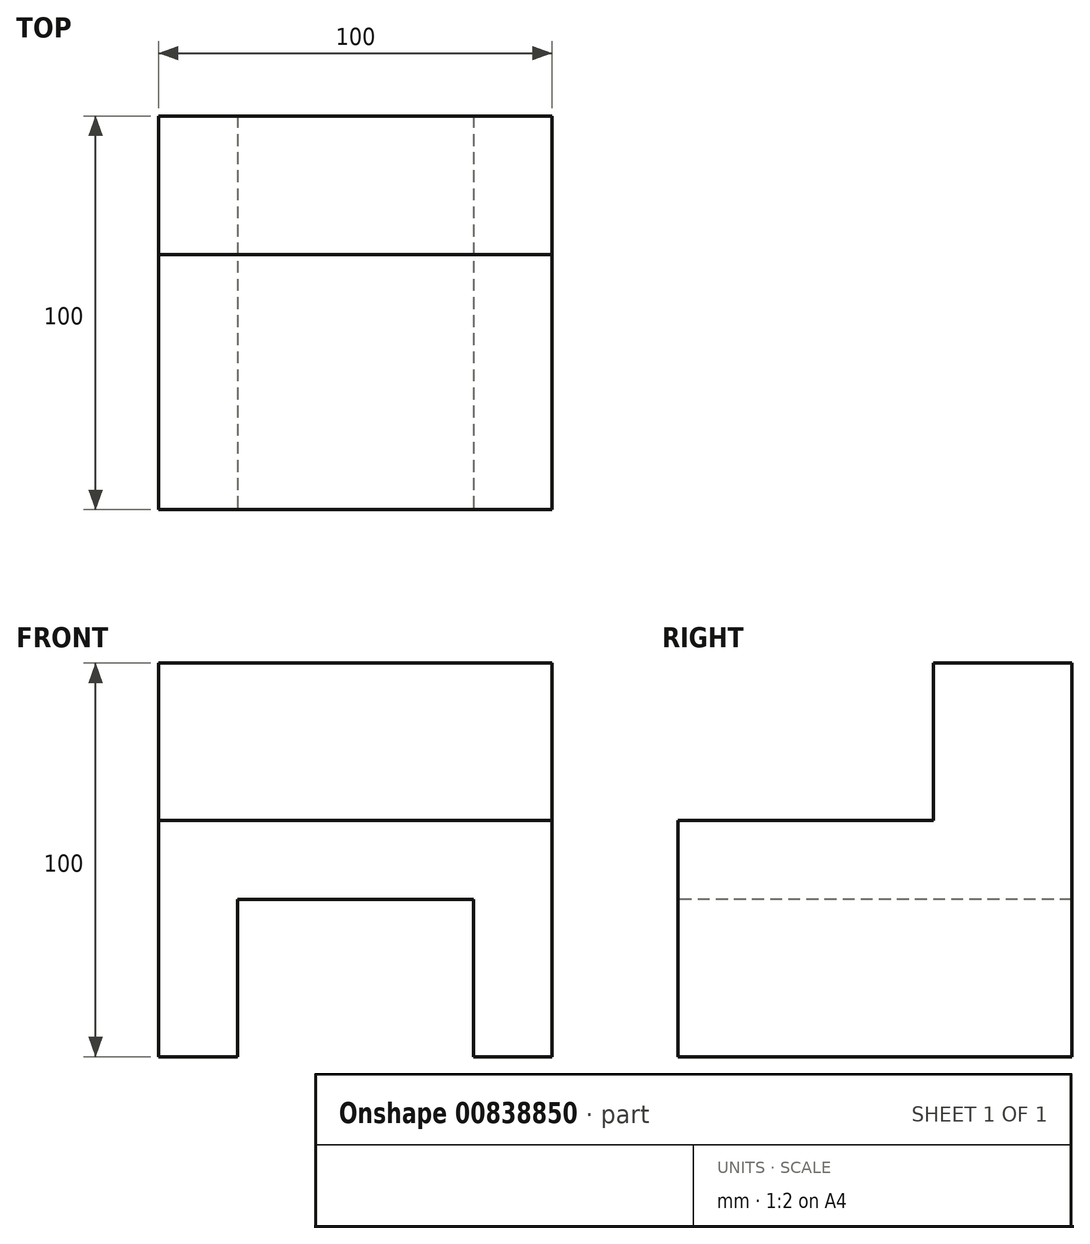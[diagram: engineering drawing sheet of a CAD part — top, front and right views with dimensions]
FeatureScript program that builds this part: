
annotation { "Feature Type Name" : "Feature", "Feature Type Description" : "" }
export const myFeature = defineFeature(function(context is Context, id is Id, definition is map)
    precondition{}
    {
        {
            var Q0;
            Q0=qCreatedBy(makeId("Top.planeOp"),FACE);
            var sketch = newSketch(context, id + "F0", { "sketchPlane" : qUnion([Q0])});
            skLineSegment(sketch, "E0.bottom", {"start": v(50, -50) * mm, "end": v(-50, -50) * mm});
            skLineSegment(sketch, "E0.top", {"start": v(50, 50) * mm, "end": v(-50, 50) * mm});
            skLineSegment(sketch, "E0.left", {"start": v(50, -50) * mm, "end": v(50, 50) * mm});
            skLineSegment(sketch, "E0.right", {"start": v(-50, -50) * mm, "end": v(-50, 50) * mm});
            skPoint(sketch, "E0.middle", {"position": v(0, 0) * mm});
            skSolve(sketch);
        }
        {
            var Q0;
            Q0=makeQuery(id+"F0.imprint","IMPRINT",FACE,{"disambiguationData":[TD([[makeQuery(id+"F0.imprint","IMPRINT",EDGE,{"derivedFrom":sQuery(id+"F0.wireOp",EDGE,"E0.bottom")}),-1.0]])]});
            extrude(context, id + "F1", {"entities" : qUnion([Q0]), "depth" : 100 * mm, "offsetDistance" : 25 * mm});
        }
        {
            var Q0;
            Q0=makeQuery(id+"F1.opExtrude","CAP_FACE",FACE,{"disambiguationData":[OSD([sQuery(id+"F0.wireOp",EDGE,"E0.bottom"),sQuery(id+"F0.wireOp",EDGE,"E0.top"),sQuery(id+"F0.wireOp",EDGE,"E0.left"),sQuery(id+"F0.wireOp",EDGE,"E0.right")])],"isStart":false});
            var sketch = newSketch(context, id + "F2", { "sketchPlane" : qUnion([Q0])});
            skLineSegment(sketch, "E1.bottom", {"start": v(-50, 14.8) * mm, "end": v(50, 14.8) * mm});
            skLineSegment(sketch, "E1.top", {"start": v(-50, 14.89) * mm, "end": v(50, 14.89) * mm});
            skLineSegment(sketch, "E1.left", {"start": v(-50, 14.8) * mm, "end": v(-50, 14.89) * mm});
            skLineSegment(sketch, "E1.right", {"start": v(50, 14.8) * mm, "end": v(50, 14.89) * mm});
            skSolve(sketch);
        }
        {
            var Q0;
            {var subQ0=sQuery(id+"F2.wireOp",EDGE,"E1.bottom");Q0=makeQuery(id+"F2.imprint","IMPRINT",FACE,{"disambiguationData":[TD([[makeQuery(id+"F2.imprint","IMPRINT",EDGE,{"derivedFrom":subQ0}),-1.0]])]});}
            extrude(context, id + "F3", {"entities" : qUnion([Q0]), "operationType" : NewBodyOperationType.REMOVE, "oppositeDirection" : true, "depth" : 40 * mm, "offsetDistance" : 25 * mm});
        }
        {
            var Q0;
            Q0=makeQuery(id+"F1.opExtrude","SWEPT_FACE",FACE,{"disambiguationData":[OSD([sQuery(id+"F0.wireOp",EDGE,"E0.bottom")])]});
            var sketch = newSketch(context, id + "F4", { "sketchPlane" : qUnion([Q0])});
            skLineSegment(sketch, "E2.bottom", {"start": v(-30, 40) * mm, "end": v(30, 40) * mm});
            skLineSegment(sketch, "E2.top", {"start": v(-30, 0) * mm, "end": v(30, 0) * mm});
            skLineSegment(sketch, "E2.left", {"start": v(-30, 40) * mm, "end": v(-30, 0) * mm});
            skLineSegment(sketch, "E2.right", {"start": v(30, 40) * mm, "end": v(30, 0) * mm});
            skSolve(sketch);
        }
        {
            var Q0;
            Q0=makeQuery(id+"F4.imprint","IMPRINT",FACE,{"disambiguationData":[TD([[makeQuery(id+"F4.imprint","IMPRINT",EDGE,{"derivedFrom":sQuery(id+"F4.wireOp",EDGE,"E2.bottom")}),-1.0]])]});
            extrude(context, id + "F5", {"entities" : qUnion([Q0]), "operationType" : NewBodyOperationType.REMOVE, "endBound" : BoundingType.THROUGH_ALL, "oppositeDirection" : true, "depth" : 25 * mm, "offsetDistance" : 25 * mm});
        }
    });
